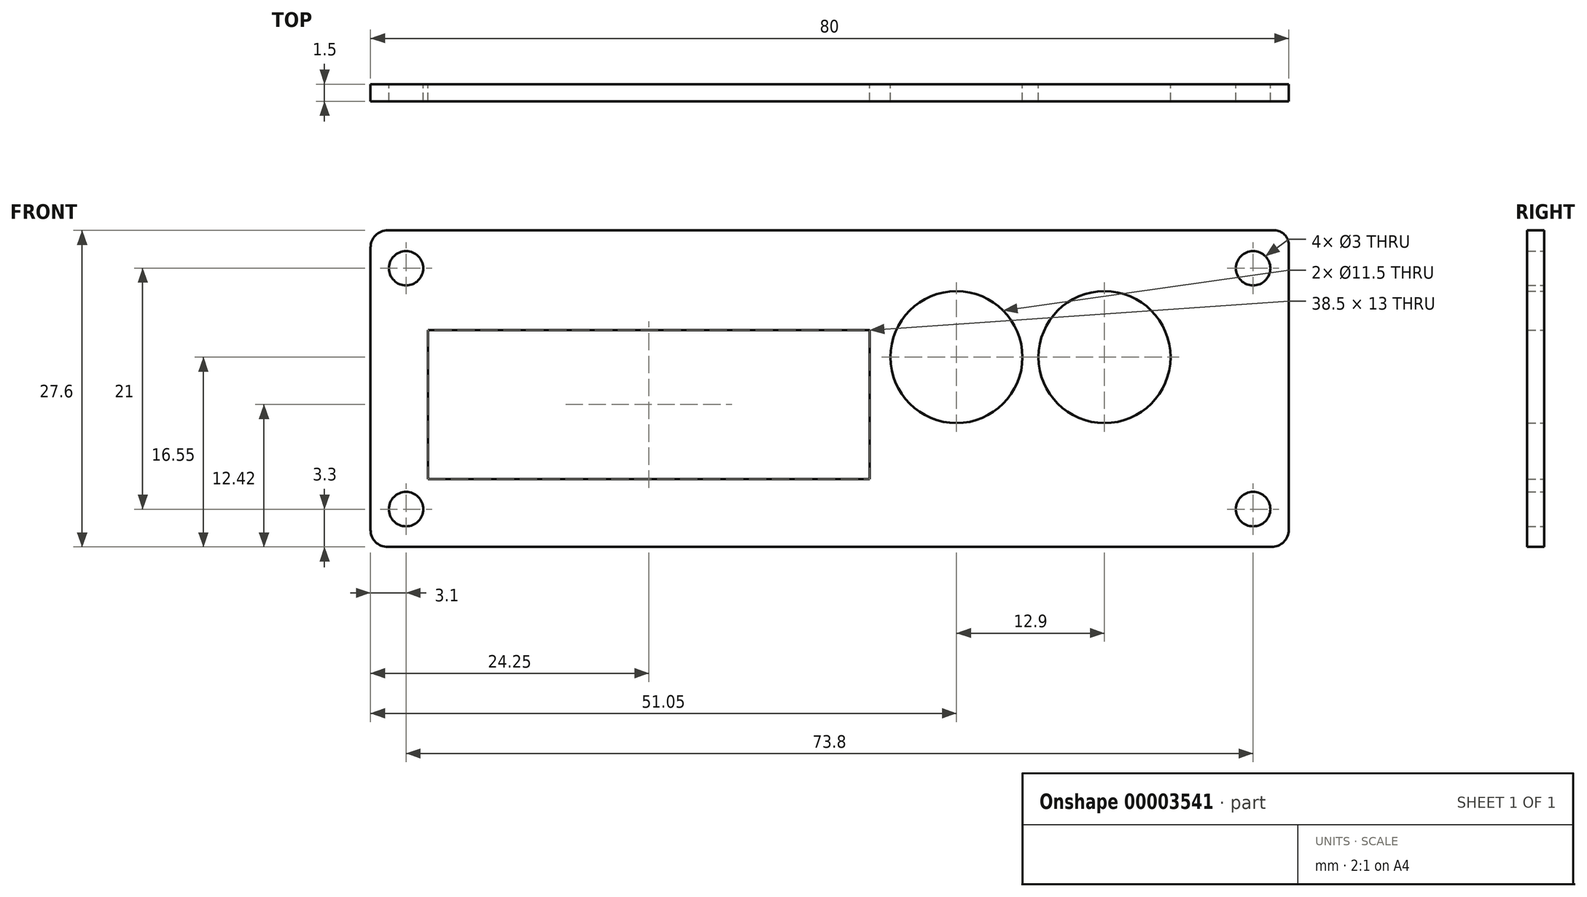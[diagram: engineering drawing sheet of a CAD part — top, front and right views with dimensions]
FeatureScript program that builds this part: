
annotation { "Feature Type Name" : "Feature", "Feature Type Description" : "" }
export const myFeature = defineFeature(function(context is Context, id is Id, definition is map)
    precondition{}
    {
        {
            var Q0;
            Q0=qCreatedBy(makeId("Front.planeOp"),FACE);
            var sketch = newSketch(context, id + "F0", { "sketchPlane" : qUnion([Q0])});
            skLineSegment(sketch, "E0.bottom", {"start": v(1.5, 0) * mm, "end": v(78.5, 0) * mm});
            skLineSegment(sketch, "E0.top", {"start": v(1.5, 27.6) * mm, "end": v(78.75, 27.6) * mm});
            skLineSegment(sketch, "E0.left", {"start": v(0, 1.5) * mm, "end": v(0, 26.1) * mm});
            skLineSegment(sketch, "E0.right", {"start": v(80, 1.5) * mm, "end": v(80, 26.35) * mm});
            skCircle(sketch, "E1", {"center": v(3.1, 3.3) * mm, "radius": 1.5 * mm});
            skCircle(sketch, "E2", {"center": v(76.9, 3.3) * mm, "radius": 1.5 * mm});
            skCircle(sketch, "E3", {"center": v(76.9, 24.3) * mm, "radius": 1.5 * mm});
            skCircle(sketch, "E4", {"center": v(3.1, 24.3) * mm, "radius": 1.5 * mm});
            skPoint(sketch, "E5.visualSharp", {"position": v(80, 27.6) * mm});
            skArc(sketch, "E5.filletArc", {"start": v(80, 26.35) * mm, "mid": v(79.63, 27.23) * mm, "end": v(78.75, 27.6) * mm});
            skPoint(sketch, "E6.visualSharp", {"position": v(80, 0) * mm});
            skArc(sketch, "E6.filletArc", {"start": v(78.5, 0) * mm, "mid": v(79.56, 0.44) * mm, "end": v(80, 1.5) * mm});
            skPoint(sketch, "E7.visualSharp", {"position": v(0, 27.6) * mm});
            skArc(sketch, "E7.filletArc", {"start": v(1.5, 27.6) * mm, "mid": v(0.44, 27.16) * mm, "end": v(0, 26.1) * mm});
            skPoint(sketch, "E8.visualSharp", {"position": v(0, 0) * mm});
            skArc(sketch, "E8.filletArc", {"start": v(0, 1.5) * mm, "mid": v(0.44, 0.44) * mm, "end": v(1.5, 0) * mm});
            skLineSegment(sketch, "E9.bottom", {"start": v(5, 5.92) * mm, "end": v(43.5, 5.92) * mm});
            skLineSegment(sketch, "E9.top", {"start": v(5, 18.92) * mm, "end": v(43.5, 18.92) * mm});
            skLineSegment(sketch, "E9.left", {"start": v(5, 5.92) * mm, "end": v(5, 18.92) * mm});
            skLineSegment(sketch, "E9.right", {"start": v(43.5, 5.92) * mm, "end": v(43.5, 18.92) * mm});
            skCircle(sketch, "E10", {"center": v(51.05, 16.55) * mm, "radius": 5.75 * mm});
            skCircle(sketch, "E11", {"center": v(63.95, 16.55) * mm, "radius": 5.75 * mm});
            skSolve(sketch);
        }
        {
            var Q0;
            Q0=qSketchRegion(id+"F0",true);
            extrude(context, id + "F1", {"entities" : qUnion([Q0]), "depth" : 1.5 * mm});
        }
    });
